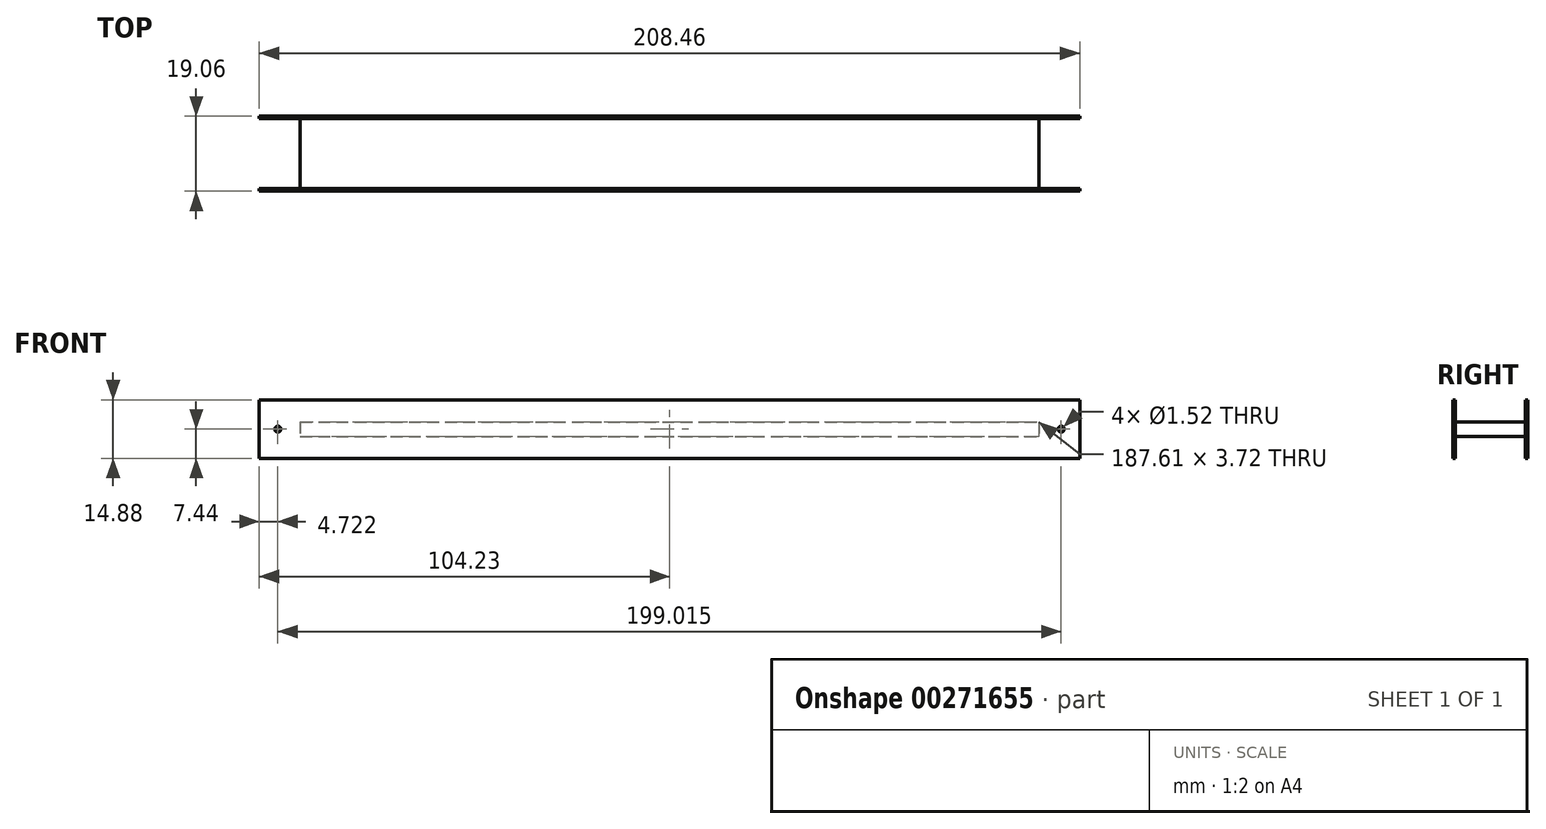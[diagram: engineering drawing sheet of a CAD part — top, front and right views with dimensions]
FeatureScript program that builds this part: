
annotation { "Feature Type Name" : "Feature", "Feature Type Description" : "" }
export const myFeature = defineFeature(function(context is Context, id is Id, definition is map)
    precondition{}
    {
        {
            var Q0;
            Q0=qCreatedBy(makeId("Front.planeOp"),FACE);
            var sketch = newSketch(context, id + "F0", { "sketchPlane" : qUnion([Q0])});
            skLineSegment(sketch, "E0.bottom", {"start": v(-104.23, 7.44) * mm, "end": v(104.23, 7.44) * mm});
            skLineSegment(sketch, "E0.top", {"start": v(-104.23, -7.44) * mm, "end": v(104.23, -7.44) * mm});
            skLineSegment(sketch, "E0.left", {"start": v(-104.23, 7.44) * mm, "end": v(-104.23, -7.44) * mm});
            skLineSegment(sketch, "E0.right", {"start": v(104.23, 7.44) * mm, "end": v(104.23, -7.44) * mm});
            skPoint(sketch, "E0.middle", {"position": v(0, 0) * mm});
            skLineSegment(sketch, "E1.bottom", {"start": v(-93.8, 1.86) * mm, "end": v(93.8, 1.86) * mm});
            skLineSegment(sketch, "E1.top", {"start": v(-93.8, -1.86) * mm, "end": v(93.8, -1.86) * mm});
            skLineSegment(sketch, "E1.left", {"start": v(-93.8, 1.86) * mm, "end": v(-93.8, -1.86) * mm});
            skLineSegment(sketch, "E1.right", {"start": v(93.8, 1.86) * mm, "end": v(93.8, -1.86) * mm});
            skCircle(sketch, "E2", {"center": v(-99.5, 0) * mm, "radius": 0.76 * mm});
            skCircle(sketch, "E3.MirrorC", {"center": v(99.5, 0) * mm, "radius": 0.76 * mm});
            skSolve(sketch);
        }
        {
            var Q0;
            Q0=makeQuery(id+"F0.imprint","IMPRINT",FACE,{"disambiguationData":[TD([[makeQuery(id+"F0.imprint","IMPRINT",EDGE,{"derivedFrom":sQuery(id+"F0.wireOp",EDGE,"E0.bottom")}),-1.0]])]});
            var Q1;
            Q1=makeQuery(id+"F0.imprint","IMPRINT",FACE,{"disambiguationData":[TD([[makeQuery(id+"F0.imprint","IMPRINT",EDGE,{"derivedFrom":sQuery(id+"F0.wireOp",EDGE,"E1.bottom")}),-1.0]])]});
            extrude(context, id + "F1", {"entities" : qUnion([Q0, Q1]), "endBound" : BoundingType.SYMMETRIC, "depth" : 19.05 * mm});
        }
        {
            var Q0;
            Q0=makeQuery(id+"F0.imprint","IMPRINT",FACE,{"disambiguationData":[TD([[makeQuery(id+"F0.imprint","IMPRINT",EDGE,{"derivedFrom":sQuery(id+"F0.wireOp",EDGE,"E0.bottom")}),-1.0]])]});
            extrude(context, id + "F2", {"entities" : qUnion([Q0]), "operationType" : NewBodyOperationType.REMOVE, "endBound" : BoundingType.SYMMETRIC, "oppositeDirection" : true, "depth" : 17.78 * mm});
        }
    });
